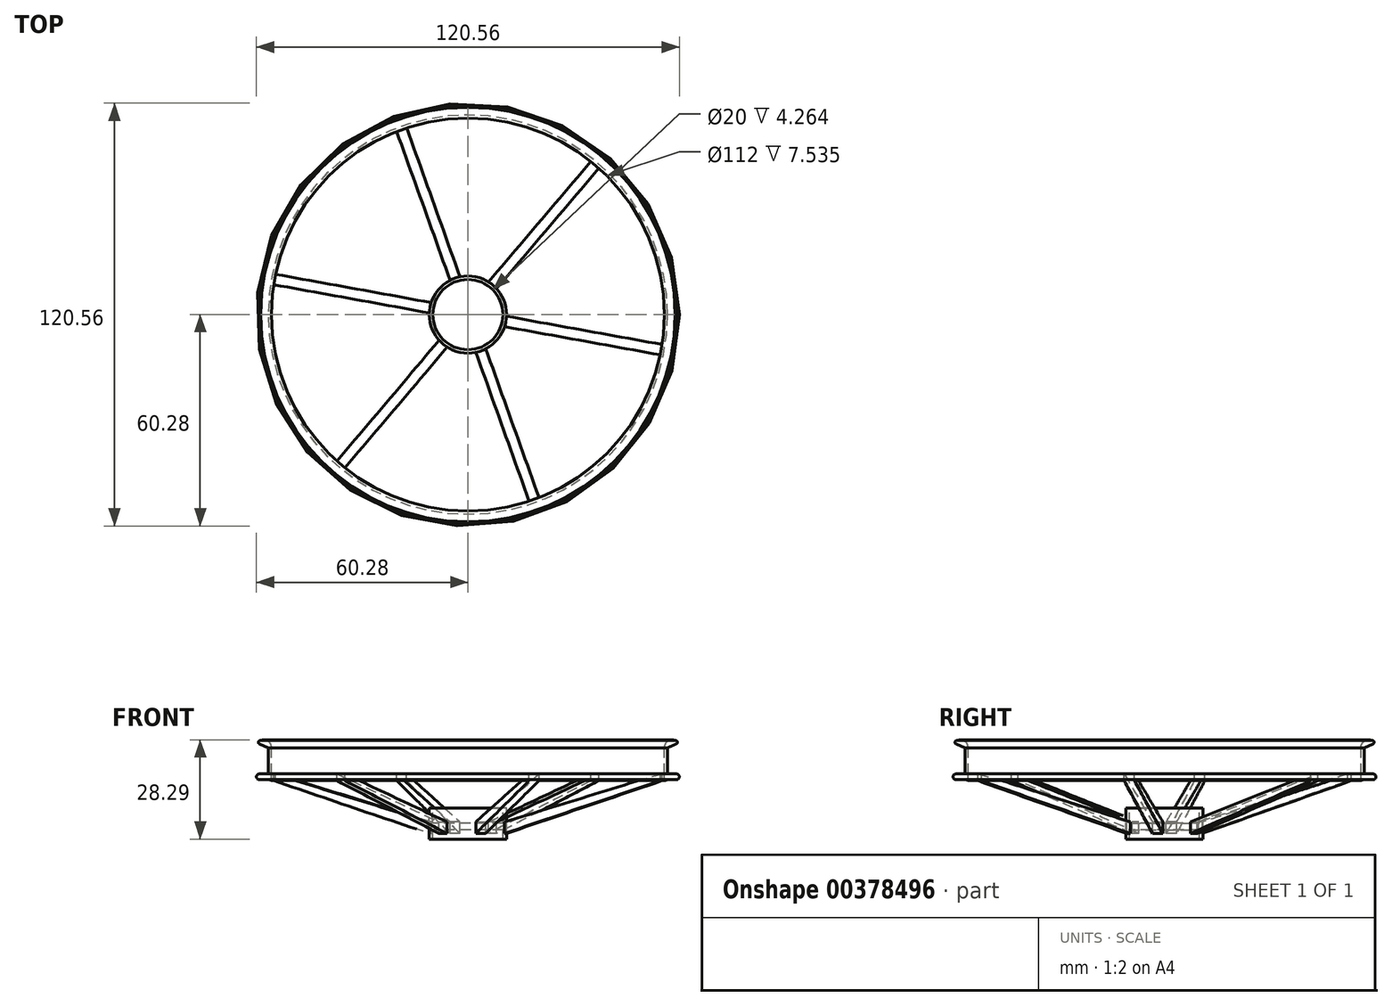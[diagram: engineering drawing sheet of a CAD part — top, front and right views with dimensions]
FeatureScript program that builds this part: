
annotation { "Feature Type Name" : "Feature", "Feature Type Description" : "" }
export const myFeature = defineFeature(function(context is Context, id is Id, definition is map)
    precondition{}
    {
        {
            var Q0;
            Q0=qCreatedBy(makeId("Top.planeOp"),FACE);
            var sketch = newSketch(context, id + "F0", { "sketchPlane" : qUnion([Q0])});
            skLineSegment(sketch, "E0.bottom", {"start": v(65, -65) * mm, "end": v(-65, -65) * mm, "construction": true});
            skLineSegment(sketch, "E0.top", {"start": v(65, 65) * mm, "end": v(-65, 65) * mm, "construction": true});
            skLineSegment(sketch, "E0.left", {"start": v(65, -65) * mm, "end": v(65, 65) * mm, "construction": true});
            skLineSegment(sketch, "E0.right", {"start": v(-65, -65) * mm, "end": v(-65, 65) * mm, "construction": true});
            skPoint(sketch, "E0.middle", {"position": v(0, 0) * mm});
            skCircle(sketch, "E1", {"center": v(-65, 65) * mm, "radius": 56 * mm});
            skCircle(sketch, "E2", {"center": v(65, 65) * mm, "radius": 56 * mm});
            skCircle(sketch, "E3", {"center": v(65, -65) * mm, "radius": 56 * mm});
            skCircle(sketch, "E4", {"center": v(-65, -65) * mm, "radius": 56 * mm});
            skLineSegment(sketch, "E5.bottom", {"start": v(16.5, -16.5) * mm, "end": v(-16.5, -16.5) * mm, "construction": true});
            skLineSegment(sketch, "E5.top", {"start": v(16.5, 16.5) * mm, "end": v(-16.5, 16.5) * mm, "construction": true});
            skLineSegment(sketch, "E5.left", {"start": v(16.5, -16.5) * mm, "end": v(16.5, 16.5) * mm, "construction": true});
            skLineSegment(sketch, "E5.right", {"start": v(-16.5, -16.5) * mm, "end": v(-16.5, 16.5) * mm, "construction": true});
            skSolve(sketch);
        }
        {
            var Q0;
            Q0=qCreatedBy(makeId("Front.planeOp"),FACE);
            cPlane(context, id + "F1", {"entities" : qUnion([Q0]), "cplaneType" : CPlaneType.OFFSET, "offset" : 65 * mm, "width" : 150 * mm, "height" : 150 * mm});
        }
        {
            var Q0;
            Q0=qCreatedBy(id+"F1.planeOp",FACE);
            var sketch = newSketch(context, id + "F2", { "sketchPlane" : qUnion([Q0])});
            skLineSegment(sketch, "E6", {"start": v(-65, 0) * mm, "end": v(-121, 0) * mm, "construction": true});
            skLineSegment(sketch, "E7", {"start": v(-65, 0) * mm, "end": v(-65, -14) * mm, "construction": true});
            skLineSegment(sketch, "E8", {"start": v(-65, -14) * mm, "end": v(-75, -14) * mm});
            skLineSegment(sketch, "E9", {"start": v(-76, -13.7) * mm, "end": v(-121, 0) * mm});
            skLineSegment(sketch, "E10", {"start": v(-121, 0) * mm, "end": v(-121, 7.54) * mm});
            skLineSegment(sketch, "E11", {"start": v(-121.9, 7.44) * mm, "end": v(-121.9, 0) * mm});
            skLineSegment(sketch, "E12", {"start": v(-75.04, -15.93) * mm, "end": v(-65, -15.93) * mm});
            skLineSegment(sketch, "E13", {"start": v(-75, -14) * mm, "end": v(-75, -9.74) * mm});
            skLineSegment(sketch, "E14", {"start": v(-75, -9.74) * mm, "end": v(-76, -9.74) * mm});
            skLineSegment(sketch, "E15", {"start": v(-76, -9.74) * mm, "end": v(-76, -13.7) * mm});
            skLineSegment(sketch, "E16", {"start": v(-76, -16.95) * mm, "end": v(-76, -18.59) * mm});
            skLineSegment(sketch, "E17", {"start": v(-76, -18.59) * mm, "end": v(-75, -18.59) * mm});
            skLineSegment(sketch, "E18", {"start": v(-75, -18.59) * mm, "end": v(-75.04, -15.93) * mm});
            skLineSegment(sketch, "E19", {"start": v(-121.9, -1.63) * mm, "end": v(-76, -16.95) * mm});
            skLineSegment(sketch, "E20", {"start": v(-121.9, 7.44) * mm, "end": v(-124.44, 8.56) * mm});
            skArc(sketch, "E21", {"start": v(-121, 7.54) * mm, "mid": v(-122, 9.36) * mm, "end": v(-124.09, 9.5) * mm});
            skArc(sketch, "E22", {"start": v(-124.09, 9.5) * mm, "mid": v(-124.7, 9.2) * mm, "end": v(-124.44, 8.56) * mm});
            skLineSegment(sketch, "E23", {"start": v(-121.9, -1.63) * mm, "end": v(-124.45, -1.63) * mm});
            skLineSegment(sketch, "E24", {"start": v(-121.9, 0) * mm, "end": v(-124.46, 0) * mm});
            skArc(sketch, "E25", {"start": v(-124.46, 0) * mm, "mid": v(-125.28, -0.82) * mm, "end": v(-124.45, -1.63) * mm});
            skLineSegment(sketch, "E26", {"start": v(-65, -15.93) * mm, "end": v(-65, -14) * mm});
            skSolve(sketch);
        }
        {
            var Q0;
            Q0 = qSketchRegion(id + "F2", true);
            var Q1;
            Q1=sQuery(id+"F2.wireOp",EDGE,"E7");
            revolve(context, id + "F3", {"entities" : qUnion([Q0]), "axis" : qUnion([Q1]), "revolveType" : RevolveType.FULL});
        }
        {
            var Q0;
            Q0=qCreatedBy(makeId("Top.planeOp"),FACE);
            var sketch = newSketch(context, id + "F4", { "sketchPlane" : qUnion([Q0])});
            skArc(sketch, "E27", {"start": v(-54.01, -65.47) * mm, "mid": v(-54.64, -61.3) * mm, "end": v(-56.8, -57.66) * mm});
            skLineSegment(sketch, "E28", {"start": v(-101.22, -107.7) * mm, "end": v(-28.78, -22.3) * mm, "construction": true});
            skLineSegment(sketch, "E29", {"start": v(-83.87, -12.28) * mm, "end": v(-65, -65) * mm, "construction": true});
            skLineSegment(sketch, "E30", {"start": v(-120.1, -54.98) * mm, "end": v(-9.9, -75.02) * mm, "construction": true});
            skLineSegment(sketch, "E31.0", {"start": v(-85.29, -12.78) * mm, "end": v(-70.08, -55.25) * mm});
            skLineSegment(sketch, "E32.MirrorCS", {"start": v(-82.46, -11.77) * mm, "end": v(-67.26, -54.23) * mm});
            skLineSegment(sketch, "E33.MirrorCS", {"start": v(-9.63, -73.54) * mm, "end": v(-54.01, -65.47) * mm});
            skLineSegment(sketch, "E34.MirrorCS", {"start": v(-10.17, -76.5) * mm, "end": v(-54.55, -68.43) * mm});
            skLineSegment(sketch, "E35.MirrorCS", {"start": v(-100.08, -108.68) * mm, "end": v(-70.9, -74.28) * mm});
            skLineSegment(sketch, "E36.MirrorCS", {"start": v(-102.37, -106.74) * mm, "end": v(-73.2, -72.34) * mm});
            skLineSegment(sketch, "E37.trimOffspring", {"start": v(-59.1, -55.72) * mm, "end": v(-29.92, -21.32) * mm});
            skLineSegment(sketch, "E38.trimOffspring", {"start": v(-56.8, -57.66) * mm, "end": v(-27.63, -23.26) * mm});
            skLineSegment(sketch, "E39.trimOffspring", {"start": v(-59.92, -74.75) * mm, "end": v(-44.71, -117.22) * mm});
            skLineSegment(sketch, "E40.trimOffspring", {"start": v(-62.74, -75.77) * mm, "end": v(-47.54, -118.23) * mm});
            skLineSegment(sketch, "E41.trimOffspring", {"start": v(-75.99, -64.53) * mm, "end": v(-120.37, -56.46) * mm});
            skLineSegment(sketch, "E42.trimOffspring", {"start": v(-75.45, -61.57) * mm, "end": v(-119.83, -53.5) * mm});
            skLineSegment(sketch, "E43.trimOffspring", {"start": v(-64.42, -66.63) * mm, "end": v(-46.13, -117.72) * mm, "construction": true});
            skArc(sketch, "E44", {"start": v(-85.29, -12.78) * mm, "mid": v(-107.72, -28.76) * mm, "end": v(-119.83, -53.5) * mm});
            skArc(sketch, "E45.trimOffspring", {"start": v(-29.92, -21.32) * mm, "mid": v(-54.98, -9.88) * mm, "end": v(-82.46, -11.77) * mm});
            skArc(sketch, "E46.trimOffspring", {"start": v(-9.63, -73.54) * mm, "mid": v(-12.26, -46.12) * mm, "end": v(-27.63, -23.26) * mm});
            skArc(sketch, "E47.trimOffspring", {"start": v(-100.08, -108.68) * mm, "mid": v(-75.02, -120.12) * mm, "end": v(-47.54, -118.23) * mm});
            skArc(sketch, "E48.trimOffspring", {"start": v(-120.37, -56.46) * mm, "mid": v(-117.74, -83.88) * mm, "end": v(-102.37, -106.74) * mm});
            skArc(sketch, "E49.trimOffspring", {"start": v(-44.71, -117.22) * mm, "mid": v(-22.28, -101.24) * mm, "end": v(-10.17, -76.5) * mm});
            skArc(sketch, "E50.trimOffspring", {"start": v(-59.92, -74.75) * mm, "mid": v(-56.61, -72.12) * mm, "end": v(-54.55, -68.43) * mm});
            skArc(sketch, "E51.trimOffspring", {"start": v(-70.9, -74.28) * mm, "mid": v(-66.97, -75.82) * mm, "end": v(-62.74, -75.77) * mm});
            skArc(sketch, "E52.trimOffspring", {"start": v(-75.99, -64.53) * mm, "mid": v(-75.36, -68.7) * mm, "end": v(-73.2, -72.34) * mm});
            skArc(sketch, "E53.trimOffspring", {"start": v(-70.08, -55.25) * mm, "mid": v(-73.39, -57.88) * mm, "end": v(-75.45, -61.57) * mm});
            skArc(sketch, "E54.trimOffspring", {"start": v(-59.1, -55.72) * mm, "mid": v(-63.03, -54.18) * mm, "end": v(-67.26, -54.23) * mm});
            skSolve(sketch);
        }
        {
            var Q0;
            Q0 = qSketchRegion(id + "F4", true);
            extrude(context, id + "F5", {"entities" : qUnion([Q0]), "operationType" : NewBodyOperationType.REMOVE, "oppositeDirection" : true, "depth" : 25 * mm});
        }
    });
